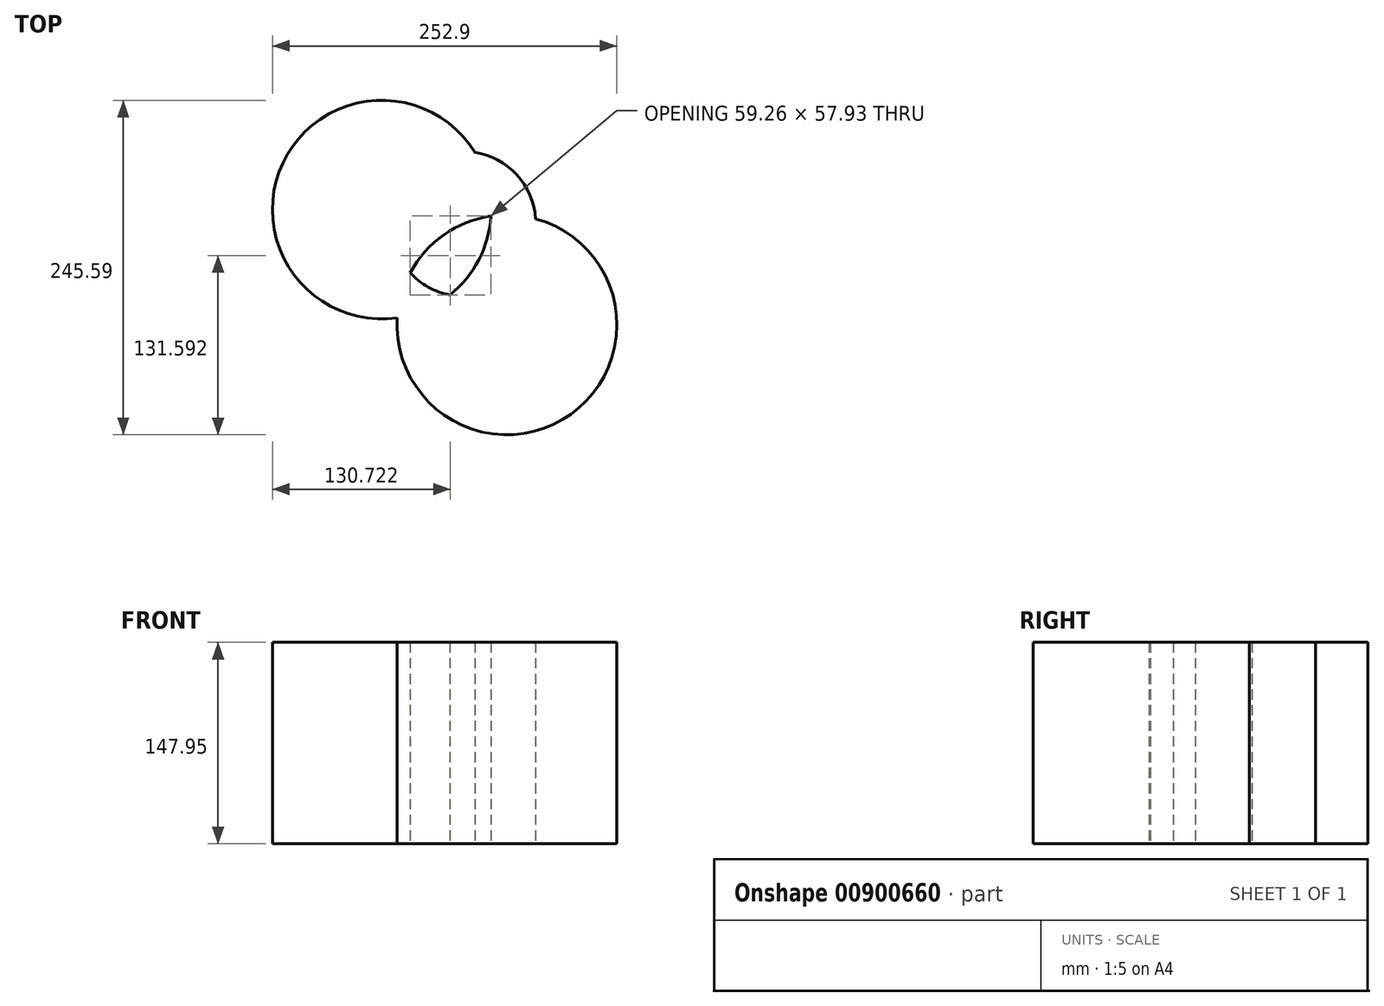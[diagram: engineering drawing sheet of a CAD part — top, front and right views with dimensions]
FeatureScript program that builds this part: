
annotation { "Feature Type Name" : "Feature", "Feature Type Description" : "" }
export const myFeature = defineFeature(function(context is Context, id is Id, definition is map)
    precondition{}
    {
        {
            var Q0;
            Q0=qCreatedBy(makeId("Top.planeOp"),FACE);
            var sketch = newSketch(context, id + "F0", { "sketchPlane" : qUnion([Q0])});
            skCircle(sketch, "E0", {"center": v(-64.38, -204.84) * mm, "radius": 80.71 * mm});
            skCircle(sketch, "E1", {"center": v(-96.3, -130.7) * mm, "radius": 53.16 * mm});
            skCircle(sketch, "E2", {"center": v(-156.32, -120.2) * mm, "radius": 80.25 * mm});
            skSolve(sketch);
        }
        {
            var Q0;
            {var subQ0=sQuery(id+"F0.wireOp",EDGE,"E2");var subQ1=sQuery(id+"F0.wireOp",EDGE,"E0");var subQ2=makeQuery(id+"F0.imprint","INTERSECT",VERTEX,{"disambiguationData":[OD(0.0)],"derivedFrom":[subQ1,subQ0]});Q0=makeQuery(id+"F0.imprint","IMPRINT",FACE,{"disambiguationData":[TD([[makeQuery(id+"F0.imprint","IMPRINT",EDGE,{"disambiguationData":[TD([[subQ2,1.0]])],"derivedFrom":subQ1}),-1.0]])]});}
            var Q1;
            {var subQ0=sQuery(id+"F0.wireOp",EDGE,"E1");var subQ1=sQuery(id+"F0.wireOp",EDGE,"E0");var subQ2=makeQuery(id+"F0.imprint","INTERSECT",VERTEX,{"disambiguationData":[OD(0.0)],"derivedFrom":[subQ1,subQ0]});Q1=makeQuery(id+"F0.imprint","IMPRINT",FACE,{"disambiguationData":[TD([[makeQuery(id+"F0.imprint","IMPRINT",EDGE,{"disambiguationData":[TD([[subQ2,-1.0]])],"derivedFrom":subQ1}),1.0]])]});}
            var Q2;
            {var subQ0=sQuery(id+"F0.wireOp",EDGE,"E2");var subQ1=sQuery(id+"F0.wireOp",EDGE,"E0");var subQ2=makeQuery(id+"F0.imprint","INTERSECT",VERTEX,{"disambiguationData":[OD(0.0)],"derivedFrom":[subQ1,subQ0]});Q2=makeQuery(id+"F0.imprint","IMPRINT",FACE,{"disambiguationData":[TD([[makeQuery(id+"F0.imprint","IMPRINT",EDGE,{"disambiguationData":[TD([[subQ2,1.0]])],"derivedFrom":subQ1}),1.0]])]});}
            var Q3;
            {var subQ0=sQuery(id+"F0.wireOp",EDGE,"E1");var subQ1=sQuery(id+"F0.wireOp",EDGE,"E0");var subQ2=makeQuery(id+"F0.imprint","INTERSECT",VERTEX,{"disambiguationData":[OD(0.0)],"derivedFrom":[subQ1,subQ0]});Q3=makeQuery(id+"F0.imprint","IMPRINT",FACE,{"disambiguationData":[TD([[makeQuery(id+"F0.imprint","IMPRINT",EDGE,{"disambiguationData":[TD([[subQ2,-1.0]])],"derivedFrom":subQ1}),-1.0]])]});}
            var Q4;
            {var subQ0=sQuery(id+"F0.wireOp",EDGE,"E2");var subQ1=sQuery(id+"F0.wireOp",EDGE,"E0");var subQ2=makeQuery(id+"F0.imprint","INTERSECT",VERTEX,{"disambiguationData":[OD(1.0)],"derivedFrom":[subQ1,subQ0]});Q4=makeQuery(id+"F0.imprint","IMPRINT",FACE,{"disambiguationData":[TD([[makeQuery(id+"F0.imprint","IMPRINT",EDGE,{"disambiguationData":[TD([[subQ2,-1.0]])],"derivedFrom":subQ1}),-1.0]])]});}
            var Q5;
            {var subQ0=sQuery(id+"F0.wireOp",EDGE,"E1");var subQ1=sQuery(id+"F0.wireOp",EDGE,"E0");var subQ2=makeQuery(id+"F0.imprint","INTERSECT",VERTEX,{"disambiguationData":[OD(0.0)],"derivedFrom":[subQ1,subQ0]});Q5=makeQuery(id+"F0.imprint","IMPRINT",FACE,{"disambiguationData":[TD([[makeQuery(id+"F0.imprint","IMPRINT",EDGE,{"disambiguationData":[TD([[subQ2,1.0]])],"derivedFrom":subQ1}),1.0]])]});}
            extrude(context, id + "F1", {"entities" : qUnion([Q0, Q1, Q2, Q3, Q4, Q5]), "depth" : 147.95 * mm, "offsetDistance" : 25.4 * mm});
        }
    });
